# Revit family: 0047972 Sylvania Lighting Fixture START eco Flood Flat IP65 6500lm 830
name_source: partatom
category: Lighting Fixtures
revit_build: Autodesk Revit 2016 (Build: 20150220_1215(x64)
units: mm (PartAtom-declared; Revit-internal decimal feet)

## family parameters
Cut with Voids When Loaded = No
Host = Face
Light Source = No
OmniClass Number = 23.80.70.00
OmniClass Title = Lighting
Part Type = Normal
Room Calculation Point = No
Round Connector Dimension = Use Diameter
Shared = No

## types (1)
- 0047972 ST E FLD FLT IP65 6500LM 830
    10W_SYL = No
    30W_SYL = No
    50W_SYL = No
    Apparent Load = 70 VA
    Assembly Code = D5020200
    AssetType = Fixed
    ClassificationName = Uniclass2015
    ClassificationValue = EF_70_80
    Cost = 0 $
    Default Elevation = 1219 mm
    DepthBracket_SYL = 25 mm  [stored 0.082021 ft]
    Description = The new Start eco Flood Flat comes with improved design. The streamlined, durable, lightweight die-cast aluminium body makes it a perfect choice for building facades, car parks, garages and construction areas. The product includes 1 m pre-wired stripped cable and fitting bracket for quick and easy installation and the universal mounting bracket allows wall or surface mounting with the possibility of vertical tilting. Black die-cast aluminum housing, white reflector, 6300 lm, 70 W, 90 lm/W, 3000K, drive current 270 mA, non dimmable, CRI>80, IP65, IK07, Class I, lumen maintenance L70:B50: 30000 hrs, 283 x 263 x 44 mm (L x W x H). Weight: 1.775kg. Energy class: A++ A+ A.
    DocumentationLiterature = http://www.sylvania-lighting.com
    DurationUnit = hours
    ElectricShockClassification = Class I
    ExpectedLife = 30000
    HeightBracket_SYL = 141 mm
    IfcExportAs = IfcLightFixtureType
    IfcExportType = IfcLightFixtureType
    ImpactProtectionIndex = IK07
    IngressProtection = IP65
    Keynote = 16500
    Lamp = LED
    LampColourRenderingIndex = 80
    LampColourTemperature = 3000 K
    LampNominalLuminous = 6300 lm
    LampsType = LED
    LuminousEfficacy = 90 lm/W
    Manufacturer = Feilo Sylvania
    ManufacturerName = Feilo Sylvania
    Material = adc12 housing
    Material_1_SYL = Body-Sylvania-FloodFlat-Black
    Model = START eco Flood Flat IP65 6500lm 830
    ModelNumber = 0047972
    ModelReference = START eco Flood Flat IP65 6500lm 830
    Name = START eco Flood Flat IP65 6500lm 830
    NominalDepth = 263 mm  [stored 0.862861 ft]
    NominalHeight = 44 mm  [stored 0.144357 ft]
    NominalLength = 283 mm  [stored 0.928478 ft]
    OffsetAxis_SYL = 13 mm
    PowerConsumption = 70 W
    PowerFactor = 0.9
    RadiusBracketIn_SYL = 12 mm  [stored 0.0393701 ft]
    RadiusBracket_SYL = 14 mm  [stored 0.0459318 ft]
    ThicknessBracket_SYL = 2 mm  [stored 0.00656168 ft]
    Type Image = <None>
    TypeLight_SYL = START eco Flood Flat Lamp : 0047972 ST E FLD FLT IP65 6500LM 830
    TypeName = START eco Flood Flat IP65 6500lm 830
    URL = http://www.sylvania-lighting.com
    Voltage = 0 V
    Weight = 8.875 kg
    WidthBracketIn_SYL = 263 mm  [stored 0.862861 ft]

note: [stored X ft] marks values corroborated as IEEE doubles in the binary element streams (Revit-internal decimal feet)

## geometry (parser evidence)
native form markers: Sweep x4
no freeform markers — native parametric forms only
